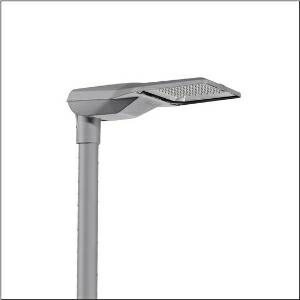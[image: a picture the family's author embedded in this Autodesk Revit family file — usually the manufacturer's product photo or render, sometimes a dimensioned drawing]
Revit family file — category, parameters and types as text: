
# Revit family: streetlight_sl_21_iq_midi___st1_0a_5xe3d41g08mb_322d
name_source: partatom
category: Lighting Fixtures
units: mm (PartAtom-declared; Revit-internal decimal feet)

## family parameters
Cut with Voids When Loaded = No
Host = Face
Light Source = No
Part Type = Normal
Room Calculation Point = No
Round Connector Dimension = Use Diameter
Shared = No

## types (1)
- --- (1 x LED, 20360 lm, 146.7 W, 4000K)
    Apparent Load = 147 VA
    CIE Flux Codes = 37 72 97 100 100
    Color Rendering = 70
    Color Temperature = 4000K
    Default Elevation = 1800 mm
    Description = Streetlight SL 21 iQ midi, mast luminaire, primary light control with lens, of PMMA, primary optical cover: cover, of toughened safety glass, transparent, light distribution: ST1.0a, light emission: direct distribution, primary light characteristic: asymmetric, installation type: post-top, side-entry, LED, High Power LED, rated luminous flux: 20.360lm, luminous efficacy: 139lm/W, light colour: 740, colour temperature: 4000K, control gear: iQ Street-Remote, control: Street-Remote, Auto-Match, Temp-Guard, Lumen-Switch, Night-Set, Smart-Wire, Light-Fading, Desk-Remote (wireless, voltage-free reading and setting of iQ features in the workshop via application-optimized NFC function/RFID function), optimised constant luminous flux control (CLO 2.0), pre-setting: linear dimming characteristic, mains connection: 230..240V, AC, 50/60Hz, start of lifetime: 147W, end of service life: 161W, reduction: 62W, luminaire housing, of diecast aluminium, powder-coated, SITECO metallic grey (DB 702S), corrosivity category C5 high according to DIN EN ISO 12944, please order mast flange separately, inclination adjustable: 0°, 5°, 10°, 15°, sealing non-destructively replaceable, multi-level sealing system, length: 644mm, width: 335mm, height: 110mm, mast flange for spigot size: 42mm (side-entry): 5XC10008XM4, 60/48mm (side-entry/post-top): 5XC10108XM2, 76/60mm (side-entry/post-top): 5XC10108XM1, mounting height: 4..8m, protection rating (complete): IP66, insulation class (complete): insulation class II (safety insulation), certification: CE, ENEC, ENEC+, VDE, impact resistance: IK10, permissible operating ambient temperature for outdoor applications: -40..+50°C, standard-compliant lighting for roads and squares, packaging unit: 1 piece

Light Distribution: ST1.0a
    Height = 111 mm
    Lamp = 1 x LED
    Lamp Light Flux = 20360 lm
    Lamp Power = 146.7 W
    Lamp count = 1
    Length = 644 mm
    Luminous efficacy = 139 lm/W
    Manufacturer = Siteco
    ModVariant = No
    Model = 5XE3D41G08MB
    Number of Poles = 1
    OnlyDefault = Yes
    Power Factor = 1
    Product Name = Streetlight SL 21 iQ midi | ST1.0a
    Product group = mast luminaire | pylon top
    ProductGroupID = 6100
    Protection Class = Protection class II
    Protection Degree = IP 66
    RLX_Detail_Level = 1
    RLX_Emergency_Light_Flux = 0 lm
    RLX_Emergency_Type = 0
    RLX_Emergency_Type_DB = No
    RlxData = <blob elided: 26941 chars, md5=071071d2>
    Socket = socket
    Standby Power = 0 W
    System Light Flux = 20360 lm
    System Power = 147 W
    Type Comments = factory setting: luminous flux: 100 % | dim-lin: 254 | 753 mA
    Type Image = l_1004298.jpg
    URL = http://relux.com
    VarID = @adj_186883
    Voltage = 0 V
    Weight = 0.00 kg
    Width = 336 mm

## geometry (parser evidence)
native form markers: Blend x4, Sweep x13
no freeform markers — native parametric forms only
